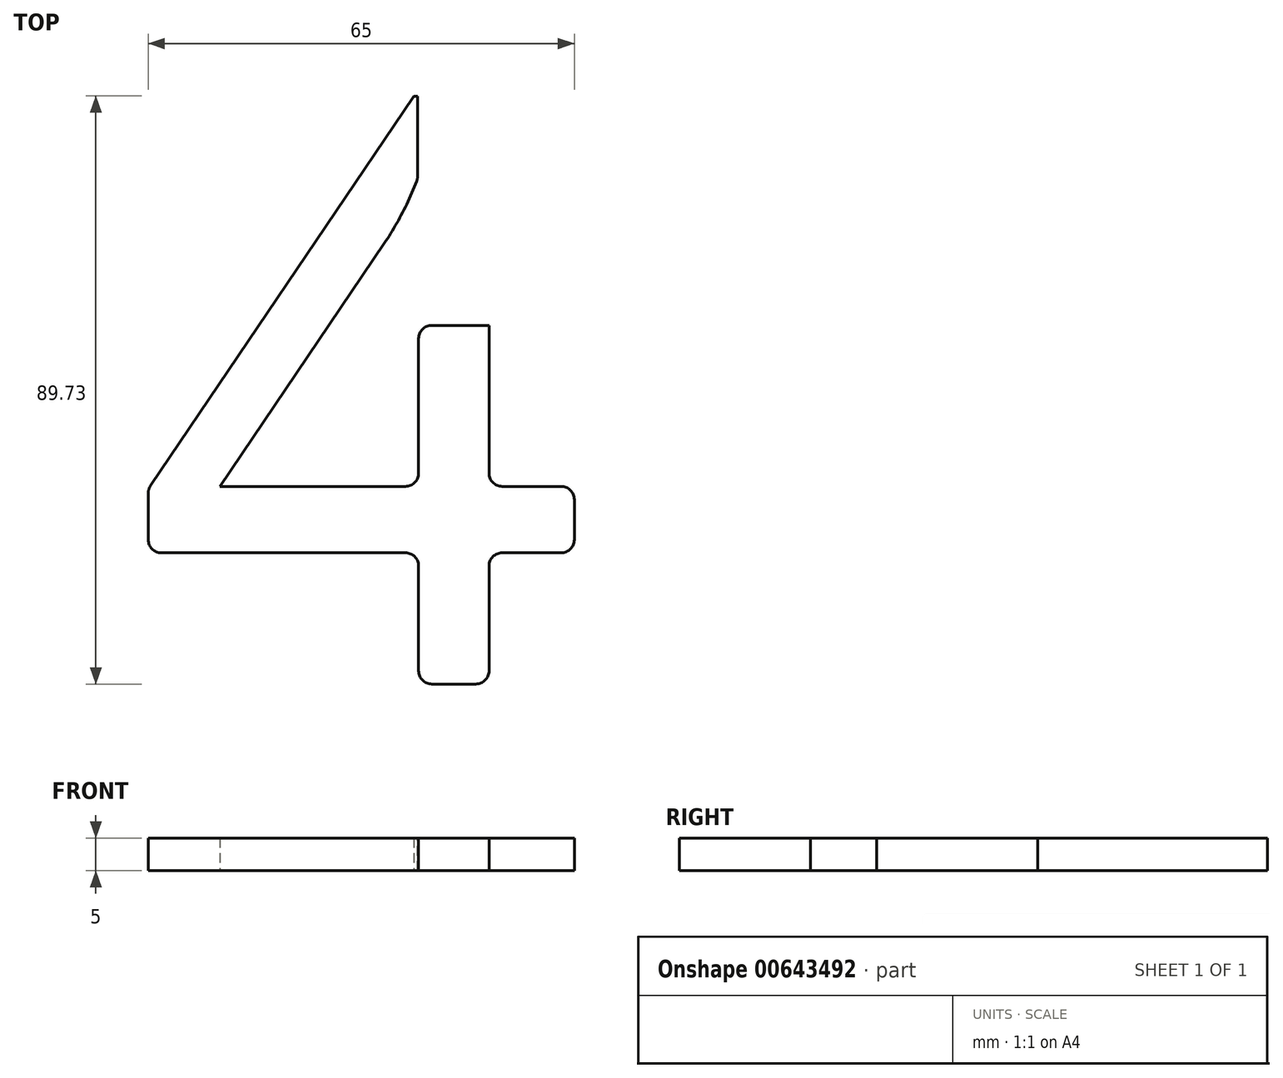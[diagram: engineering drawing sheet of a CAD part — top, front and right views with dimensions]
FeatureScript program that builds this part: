
annotation { "Feature Type Name" : "Feature", "Feature Type Description" : "" }
export const myFeature = defineFeature(function(context is Context, id is Id, definition is map)
    precondition{}
    {
        {
            var Q0;
            Q0=qCreatedBy(makeId("Top.planeOp"),FACE);
            var sketch = newSketch(context, id + "F0", { "sketchPlane" : qUnion([Q0])});
            skText(sketch, "E0", { "text": "4\n", "fontName": "DroidSansMono.ttf"});
            const initialGuessF0  = {"E0": [-0.08748, 0, 1, 0, 0.09]};
            skSetInitialGuess(sketch, initialGuessF0);
            skSolve(sketch);
        }
        {
            var Q0;
            Q0 = qSketchRegion(id + "F0", true);
            extrude(context, id + "F1", {"entities" : qUnion([Q0]), "depth" : 5 * mm, "offsetDistance" : 25 * mm});
        }
        {
            var Q0;
            Q0=makeQuery(id+"F1.opExtrude","SWEPT_FACE",FACE,{"disambiguationData":[OSD([sQuery(id+"F0.wireOp",EDGE,"E0.sketch_text.stroke-7")])]});
            var sketch = newSketch(context, id + "F2", { "sketchPlane" : qUnion([Q0])});
            skLineSegment(sketch, "E1.bottom", {"start": v(31.76, 0) * mm, "end": v(41.26, 0) * mm});
            skLineSegment(sketch, "E1.top", {"start": v(31.76, 5) * mm, "end": v(41.26, 5) * mm});
            skLineSegment(sketch, "E1.left", {"start": v(31.76, 0) * mm, "end": v(31.76, 5) * mm});
            skLineSegment(sketch, "E1.right", {"start": v(41.26, 0) * mm, "end": v(41.26, 5) * mm});
            skSolve(sketch);
        }
        {
            var Q0;
            Q0 = qSketchRegion(id + "F2", true);
            extrude(context, id + "F3", {"entities" : qUnion([Q0]), "operationType" : NewBodyOperationType.REMOVE, "oppositeDirection" : true, "depth" : 35 * mm, "offsetDistance" : 25 * mm});
        }
        {
            var Q0;
            Q0=makeQuery(id+"F3.boolean.opBoolean","COPY",FACE,{"derivedFrom":makeQuery(id+"F3.opExtrude","SWEPT_FACE",FACE,{"disambiguationData":[OSD([sQuery(id+"F2.wireOp",EDGE,"E1.right")])]})});
            var sketch = newSketch(context, id + "F4", { "sketchPlane" : qUnion([Q0])});
            skLineSegment(sketch, "E2.bottom", {"start": v(78.12, 5) * mm, "end": v(54.73, 5) * mm});
            skLineSegment(sketch, "E2.top", {"start": v(78.12, 0) * mm, "end": v(54.73, 0) * mm});
            skLineSegment(sketch, "E2.left", {"start": v(78.12, 5) * mm, "end": v(78.12, 0) * mm});
            skLineSegment(sketch, "E2.right", {"start": v(54.73, 5) * mm, "end": v(54.73, 0) * mm});
            skSolve(sketch);
        }
        {
            var Q0;
            Q0 = qSketchRegion(id + "F4", true);
            extrude(context, id + "F5", {"entities" : qUnion([Q0]), "operationType" : NewBodyOperationType.REMOVE, "oppositeDirection" : true, "depth" : 1.3 * mm, "offsetDistance" : 25 * mm});
        }
        {
            var Q0;
            Q0=makeQuery(id+"F3.boolean.opBoolean","COPY",FACE,{"derivedFrom":makeQuery(id+"F3.opExtrude","SWEPT_FACE",FACE,{"disambiguationData":[OSD([sQuery(id+"F2.wireOp",EDGE,"E1.right")])]})});
            var sketch = newSketch(context, id + "F6", { "sketchPlane" : qUnion([Q0])});
            skLineSegment(sketch, "E3.bottom", {"start": v(89.73, 5) * mm, "end": v(67, 5) * mm});
            skLineSegment(sketch, "E3.top", {"start": v(89.73, 0) * mm, "end": v(67, 0) * mm});
            skLineSegment(sketch, "E3.left", {"start": v(89.73, 5) * mm, "end": v(89.73, 0) * mm});
            skLineSegment(sketch, "E3.right", {"start": v(67, 5) * mm, "end": v(67, 0) * mm});
            skSolve(sketch);
        }
        {
            var Q0;
            Q0 = qSketchRegion(id + "F6", true);
            extrude(context, id + "F7", {"entities" : qUnion([Q0]), "operationType" : NewBodyOperationType.REMOVE, "oppositeDirection" : true, "depth" : 1.4 * mm, "offsetDistance" : 25 * mm});
        }
        {
            var Q0;
            {var subQ1=sQuery(id+"F0.wireOp",EDGE,"E0.sketch_text.stroke-15");var subQ2=sQuery(id+"F0.wireOp",EDGE,"E0.sketch_text.stroke-14");Q0=makeQuery(id+"F7.boolean.opBoolean","INTERSECT",EDGE,{"derivedFrom":[makeQuery(id+"F5.boolean.opBoolean","SPLIT",FACE,{"disambiguationData":[TD([makeQuery(id+"F1.opExtrude","SWEPT_FACE",FACE,{"disambiguationData":[OSD([subQ1])]})])],"derivedFrom":makeQuery(id+"F1.opExtrude","SWEPT_FACE",FACE,{"disambiguationData":[OSD([subQ2])]})}),makeQuery(id+"F7.opExtrude","CAP_FACE",FACE,{"disambiguationData":[OSD([sQuery(id+"F6.wireOp",EDGE,"E3.bottom"),sQuery(id+"F6.wireOp",EDGE,"E3.top"),sQuery(id+"F6.wireOp",EDGE,"E3.left"),sQuery(id+"F6.wireOp",EDGE,"E3.right")])],"isStart":false})]});}
            var Q1;
            Q1=makeQuery(id+"F1.opExtrude","SWEPT_EDGE",EDGE,{"disambiguationData":[OSD([sQuery(id+"F0.wireOp",EDGE,"E0.sketch_text.stroke-14"),sQuery(id+"F0.wireOp",EDGE,"E0.sketch_text.stroke-15")])]});
            var Q2;
            Q2=makeQuery(id+"F3.boolean.opBoolean","COPY",EDGE,{"derivedFrom":makeQuery(id+"F3.opExtrude","CAP_EDGE",EDGE,{"disambiguationData":[OSD([sQuery(id+"F2.wireOp",EDGE,"E1.left")])],"isStart":false})});
            var Q3;
            Q3=makeQuery(id+"F5.boolean.opBoolean","INTERSECT",EDGE,{"derivedFrom":[makeQuery(id+"F1.opExtrude","SWEPT_FACE",FACE,{"disambiguationData":[OSD([sQuery(id+"F0.wireOp",EDGE,"E0.sketch_text.stroke-12")])]}),makeQuery(id+"F5.opExtrude","SWEPT_FACE",FACE,{"disambiguationData":[OSD([sQuery(id+"F4.wireOp",EDGE,"E2.right")])]})]});
            var Q4;
            Q4=makeQuery(id+"F1.opExtrude","SWEPT_EDGE",EDGE,{"disambiguationData":[OSD([sQuery(id+"F0.wireOp",EDGE,"E0.sketch_text.stroke-8"),sQuery(id+"F0.wireOp",EDGE,"E0.sketch_text.stroke-9")])]});
            var Q5;
            Q5=makeQuery(id+"F1.opExtrude","SWEPT_EDGE",EDGE,{"disambiguationData":[OSD([sQuery(id+"F0.wireOp",EDGE,"E0.sketch_text.stroke-9"),sQuery(id+"F0.wireOp",EDGE,"E0.sketch_text.stroke-10")])]});
            var Q6;
            Q6=makeQuery(id+"F1.opExtrude","SWEPT_EDGE",EDGE,{"disambiguationData":[OSD([sQuery(id+"F0.wireOp",EDGE,"E0.sketch_text.stroke-0"),sQuery(id+"F0.wireOp",EDGE,"E0.sketch_text.stroke-10")])]});
            var Q7;
            Q7=makeQuery(id+"F1.opExtrude","SWEPT_EDGE",EDGE,{"disambiguationData":[OSD([sQuery(id+"F0.wireOp",EDGE,"E0.sketch_text.stroke-0"),sQuery(id+"F0.wireOp",EDGE,"E0.sketch_text.stroke-1")])]});
            var Q8;
            Q8=makeQuery(id+"F1.opExtrude","SWEPT_EDGE",EDGE,{"disambiguationData":[OSD([sQuery(id+"F0.wireOp",EDGE,"E0.sketch_text.stroke-1"),sQuery(id+"F0.wireOp",EDGE,"E0.sketch_text.stroke-2")])]});
            var Q9;
            Q9=makeQuery(id+"F1.opExtrude","SWEPT_EDGE",EDGE,{"disambiguationData":[OSD([sQuery(id+"F0.wireOp",EDGE,"E0.sketch_text.stroke-2"),sQuery(id+"F0.wireOp",EDGE,"E0.sketch_text.stroke-3")])]});
            var Q10;
            Q10=makeQuery(id+"F1.opExtrude","SWEPT_EDGE",EDGE,{"disambiguationData":[OSD([sQuery(id+"F0.wireOp",EDGE,"E0.sketch_text.stroke-3"),sQuery(id+"F0.wireOp",EDGE,"E0.sketch_text.stroke-4")])]});
            var Q11;
            Q11=makeQuery(id+"F1.opExtrude","SWEPT_EDGE",EDGE,{"disambiguationData":[OSD([sQuery(id+"F0.wireOp",EDGE,"E0.sketch_text.stroke-4"),sQuery(id+"F0.wireOp",EDGE,"E0.sketch_text.stroke-5")])]});
            var Q12;
            Q12=makeQuery(id+"F1.opExtrude","SWEPT_EDGE",EDGE,{"disambiguationData":[OSD([sQuery(id+"F0.wireOp",EDGE,"E0.sketch_text.stroke-5"),sQuery(id+"F0.wireOp",EDGE,"E0.sketch_text.stroke-6")])]});
            var Q13;
            Q13=makeQuery(id+"F1.opExtrude","SWEPT_EDGE",EDGE,{"disambiguationData":[OSD([sQuery(id+"F0.wireOp",EDGE,"E0.sketch_text.stroke-11"),sQuery(id+"F0.wireOp",EDGE,"E0.sketch_text.stroke-16")])]});
            fillet(context, id + "F8", {"entities" : qUnion([Q0, Q1, Q2, Q3, Q4, Q5, Q6, Q7, Q8, Q9, Q10, Q11, Q12, Q13]), "radius" : 2 * mm, "tangentPropagation" : true, "allowEdgeOverflow" : false});
        }
    });
